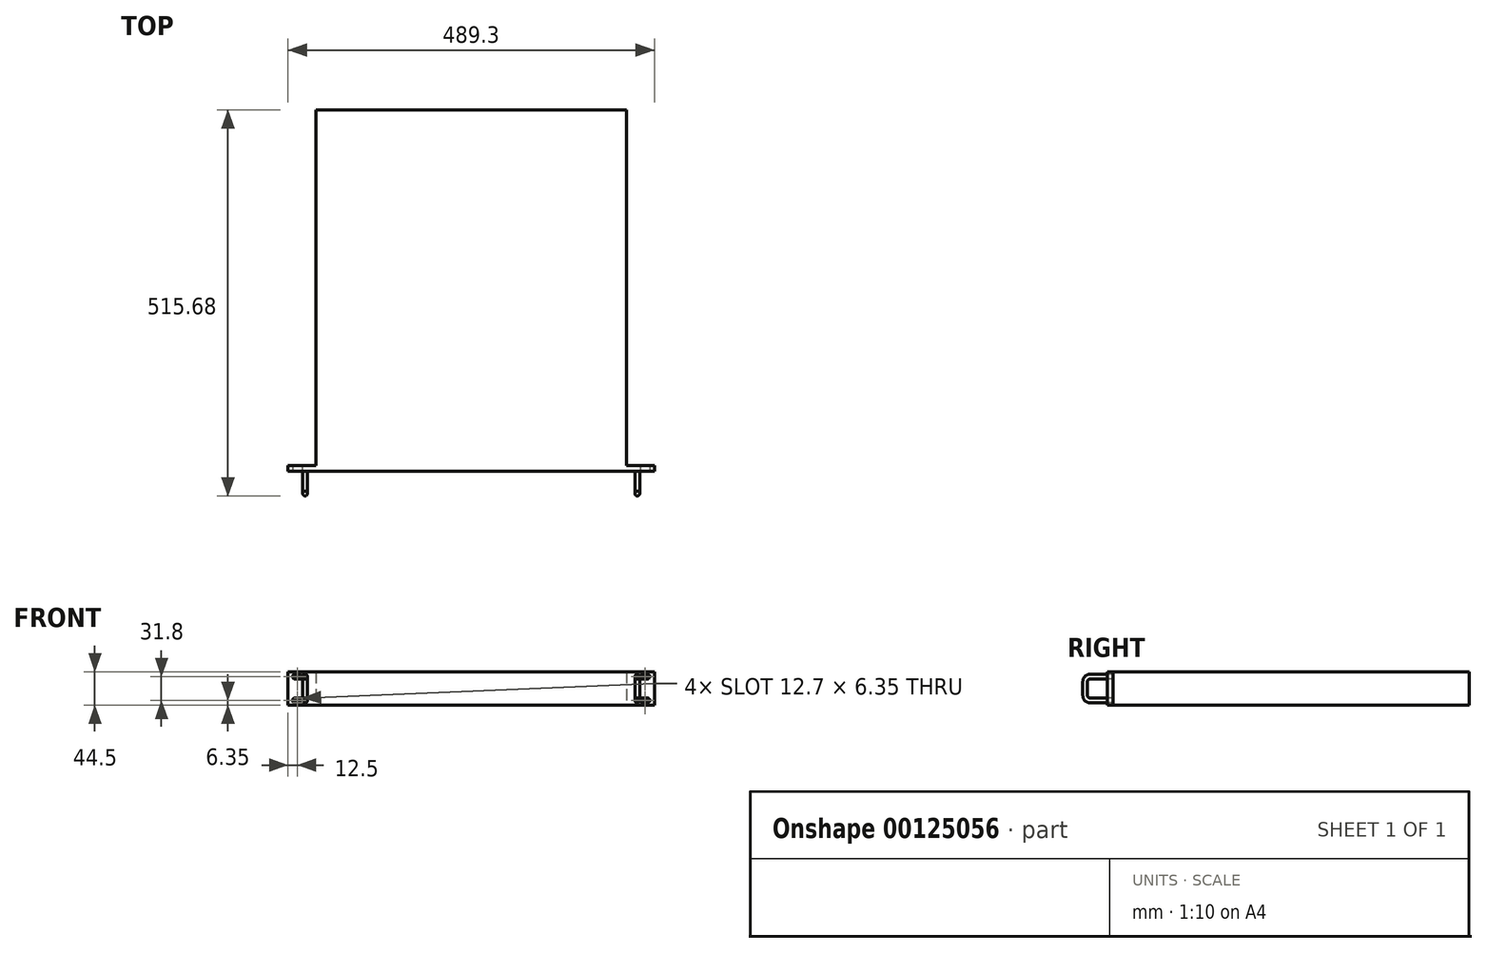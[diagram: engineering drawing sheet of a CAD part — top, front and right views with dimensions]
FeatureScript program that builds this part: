
annotation { "Feature Type Name" : "Feature", "Feature Type Description" : "" }
export const myFeature = defineFeature(function(context is Context, id is Id, definition is map)
    precondition{}
    {
        {
            var Q0;
            Q0=qCreatedBy(makeId("Front.planeOp"),FACE);
            var sketch = newSketch(context, id + "F0", { "sketchPlane" : qUnion([Q0])});
            skLineSegment(sketch, "E0.bottom", {"start": v(244.65, 22.25) * mm, "end": v(-244.65, 22.25) * mm});
            skLineSegment(sketch, "E0.top", {"start": v(244.65, -22.25) * mm, "end": v(-244.65, -22.25) * mm});
            skLineSegment(sketch, "E0.left", {"start": v(244.65, 22.25) * mm, "end": v(244.65, -22.25) * mm});
            skLineSegment(sketch, "E0.right", {"start": v(-244.65, 22.25) * mm, "end": v(-244.65, -22.25) * mm});
            skPoint(sketch, "E0.middle", {"position": v(0, 0) * mm});
            skSolve(sketch);
        }
        {
            var Q0;
            Q0=makeQuery(id+"F0.imprint","IMPRINT",FACE,{"disambiguationData":[TD([[makeQuery(id+"F0.imprint","IMPRINT",EDGE,{"derivedFrom":sQuery(id+"F0.wireOp",EDGE,"E0.bottom")}),1.0]])]});
            extrude(context, id + "F1", {"entities" : qUnion([Q0]), "oppositeDirection" : true, "depth" : 483 * mm});
        }
        {
            var Q0;
            Q0=makeQuery(id+"F1.opExtrude","CAP_FACE",FACE,{"disambiguationData":[OSD([sQuery(id+"F0.wireOp",EDGE,"E0.bottom"),sQuery(id+"F0.wireOp",EDGE,"E0.top"),sQuery(id+"F0.wireOp",EDGE,"E0.left"),sQuery(id+"F0.wireOp",EDGE,"E0.right")])],"isStart":false});
            var sketch = newSketch(context, id + "F2", { "sketchPlane" : qUnion([Q0])});
            skLineSegment(sketch, "E1.bottom", {"start": v(-244.65, 22.25) * mm, "end": v(-207.25, 22.25) * mm});
            skLineSegment(sketch, "E1.top", {"start": v(-244.65, -22.25) * mm, "end": v(-207.25, -22.25) * mm});
            skLineSegment(sketch, "E1.left", {"start": v(-244.65, 22.25) * mm, "end": v(-244.65, -22.25) * mm});
            skLineSegment(sketch, "E1.right", {"start": v(-207.25, 22.25) * mm, "end": v(-207.25, -22.25) * mm});
            skLineSegment(sketch, "E2.bottom", {"start": v(244.65, 22.25) * mm, "end": v(207.25, 22.25) * mm});
            skLineSegment(sketch, "E2.top", {"start": v(244.65, -22.25) * mm, "end": v(207.25, -22.25) * mm});
            skLineSegment(sketch, "E2.left", {"start": v(244.65, 22.25) * mm, "end": v(244.65, -22.25) * mm});
            skLineSegment(sketch, "E2.right", {"start": v(207.25, 22.25) * mm, "end": v(207.25, -22.25) * mm});
            skSolve(sketch);
        }
        {
            var Q0;
            Q0 = qSketchRegion(id + "F2", true);
            extrude(context, id + "F3", {"entities" : qUnion([Q0]), "operationType" : NewBodyOperationType.REMOVE, "oppositeDirection" : true, "depth" : 475 * mm});
        }
        {
            var Q0;
            Q0=makeQuery(id+"F1.opExtrude","CAP_FACE",FACE,{"disambiguationData":[OSD([sQuery(id+"F0.wireOp",EDGE,"E0.bottom"),sQuery(id+"F0.wireOp",EDGE,"E0.top"),sQuery(id+"F0.wireOp",EDGE,"E0.left"),sQuery(id+"F0.wireOp",EDGE,"E0.right")])],"isStart":true});
            var sketch = newSketch(context, id + "F4", { "sketchPlane" : qUnion([Q0])});
            skLineSegment(sketch, "E3.bottom", {"start": v(-228.98, 12.72) * mm, "end": v(-235.33, 12.72) * mm});
            skLineSegment(sketch, "E3.top", {"start": v(-228.98, 19.07) * mm, "end": v(-235.33, 19.07) * mm});
            skPoint(sketch, "E3.middle", {"position": v(-232.15, 15.9) * mm});
            skArc(sketch, "E4", {"start": v(-235.33, 19.07) * mm, "mid": v(-238.5, 15.9) * mm, "end": v(-235.33, 12.72) * mm});
            skArc(sketch, "E5", {"start": v(-228.98, 12.72) * mm, "mid": v(-225.8, 15.9) * mm, "end": v(-228.98, 19.07) * mm});
            skArc(sketch, "E6.0.1.0", {"start": v(-235.33, -12.73) * mm, "mid": v(-238.5, -15.9) * mm, "end": v(-235.33, -19.08) * mm});
            skArc(sketch, "E6.0.1.1", {"start": v(-228.98, -19.08) * mm, "mid": v(-225.8, -15.9) * mm, "end": v(-228.98, -12.73) * mm});
            skLineSegment(sketch, "E6.0.1.2", {"start": v(-228.98, -19.08) * mm, "end": v(-235.33, -19.08) * mm});
            skLineSegment(sketch, "E6.0.1.3", {"start": v(-228.98, -12.73) * mm, "end": v(-235.33, -12.73) * mm});
            skArc(sketch, "E6.1.0.0", {"start": v(228.98, 19.07) * mm, "mid": v(225.8, 15.9) * mm, "end": v(228.98, 12.72) * mm});
            skArc(sketch, "E6.1.0.1", {"start": v(235.33, 12.72) * mm, "mid": v(238.5, 15.9) * mm, "end": v(235.33, 19.07) * mm});
            skLineSegment(sketch, "E6.1.0.2", {"start": v(235.33, 12.72) * mm, "end": v(228.98, 12.72) * mm});
            skLineSegment(sketch, "E6.1.0.3", {"start": v(235.33, 19.07) * mm, "end": v(228.98, 19.07) * mm});
            skArc(sketch, "E6.1.1.0", {"start": v(228.98, -12.73) * mm, "mid": v(225.8, -15.9) * mm, "end": v(228.98, -19.08) * mm});
            skArc(sketch, "E6.1.1.1", {"start": v(235.33, -19.08) * mm, "mid": v(238.5, -15.9) * mm, "end": v(235.33, -12.73) * mm});
            skLineSegment(sketch, "E6.1.1.2", {"start": v(235.33, -19.08) * mm, "end": v(228.98, -19.08) * mm});
            skLineSegment(sketch, "E6.1.1.3", {"start": v(235.33, -12.73) * mm, "end": v(228.98, -12.73) * mm});
            skSolve(sketch);
        }
        {
            var Q0;
            Q0 = qSketchRegion(id + "F4", true);
            var Q1;
            Q1=makeQuery(id+"F3.boolean.opBoolean","COPY",FACE,{"derivedFrom":makeQuery(id+"F3.opExtrude","CAP_FACE",FACE,{"disambiguationData":[OSD([sQuery(id+"F2.wireOp",EDGE,"E2.bottom"),sQuery(id+"F2.wireOp",EDGE,"E2.top"),sQuery(id+"F2.wireOp",EDGE,"E2.left"),sQuery(id+"F2.wireOp",EDGE,"E2.right")])],"isStart":false})});
            extrude(context, id + "F5", {"entities" : qUnion([Q0]), "operationType" : NewBodyOperationType.REMOVE, "endBound" : BoundingType.UP_TO_SURFACE, "oppositeDirection" : true, "endBoundEntityFace" : qUnion([Q1]), "depth" : 25.4 * mm});
        }
        {
            var Q0;
            Q0=qCreatedBy(makeId("Right.planeOp"),FACE);
            cPlane(context, id + "F6", {"entities" : qUnion([Q0]), "cplaneType" : CPlaneType.OFFSET, "offset" : 228.6 * mm, "oppositeDirection" : true, "width" : 152.4 * mm, "height" : 152.4 * mm});
        }
        {
            var Q0;
            Q0=qCreatedBy(id+"F6.planeOp",FACE);
            var sketch = newSketch(context, id + "F7", { "sketchPlane" : qUnion([Q0])});
            skLineSegment(sketch, "E7", {"start": v(0, 15.9) * mm, "end": v(-23.15, 15.9) * mm});
            skLineSegment(sketch, "E8", {"start": v(-29.5, 9.55) * mm, "end": v(-29.5, -9.55) * mm});
            skLineSegment(sketch, "E9", {"start": v(-23.15, -15.9) * mm, "end": v(0, -15.9) * mm});
            skPoint(sketch, "E10.visualSharp", {"position": v(-29.5, 15.9) * mm});
            skArc(sketch, "E10.filletArc", {"start": v(-23.15, 15.9) * mm, "mid": v(-27.64, 14.04) * mm, "end": v(-29.5, 9.55) * mm});
            skPoint(sketch, "E11.visualSharp", {"position": v(-29.5, -15.9) * mm});
            skArc(sketch, "E11.filletArc", {"start": v(-29.5, -9.55) * mm, "mid": v(-27.64, -14.04) * mm, "end": v(-23.15, -15.9) * mm});
            skSolve(sketch);
        }
        {
            var Q0;
            Q0=makeQuery(id+"F1.opExtrude","CAP_FACE",FACE,{"disambiguationData":[OSD([sQuery(id+"F0.wireOp",EDGE,"E0.bottom"),sQuery(id+"F0.wireOp",EDGE,"E0.top"),sQuery(id+"F0.wireOp",EDGE,"E0.left"),sQuery(id+"F0.wireOp",EDGE,"E0.right")])],"isStart":true});
            var sketch = newSketch(context, id + "F8", { "sketchPlane" : qUnion([Q0])});
            skCircle(sketch, "E12", {"center": v(-221.8, 15.9) * mm, "radius": 3.18 * mm});
            skSolve(sketch);
        }
        {
            var Q0;
            Q0=makeQuery(id+"F8.imprint","IMPRINT",FACE,{"disambiguationData":[TD([[makeQuery(id+"F8.imprint","IMPRINT",EDGE,{"derivedFrom":sQuery(id+"F8.wireOp",EDGE,"E12")}),1.0]])]});
            var Q1;
            Q1=sQuery(id+"F7.wireOp",EDGE,"E7");
            var Q2;
            Q2=sQuery(id+"F7.wireOp",EDGE,"E10.filletArc");
            var Q3;
            Q3=sQuery(id+"F7.wireOp",EDGE,"E8");
            var Q4;
            Q4=sQuery(id+"F7.wireOp",EDGE,"E11.filletArc");
            var Q5;
            Q5=sQuery(id+"F7.wireOp",EDGE,"E9");
            sweep(context, id + "F9", {"profiles" : qUnion([Q0]), "path" : qUnion([Q1, Q2, Q3, Q4, Q5])});
        }
        {
            var Q0;
            Q0=makeQuery(id+"F9.opSweep","SWEPT_BODY",BODY,{"disambiguationData":[OSD([sQuery(id+"F7.wireOp",EDGE,"E9"),sQuery(id+"F8.wireOp",EDGE,"E12")])]});
            var Q1;
            Q1=qCreatedBy(makeId("Right.planeOp"),FACE);
            mirror(context, id + "F10", {"operationType" : NewBodyOperationType.ADD, "entities" : qUnion([Q0]), "mirrorPlane" : qUnion([Q1])});
        }
    });
